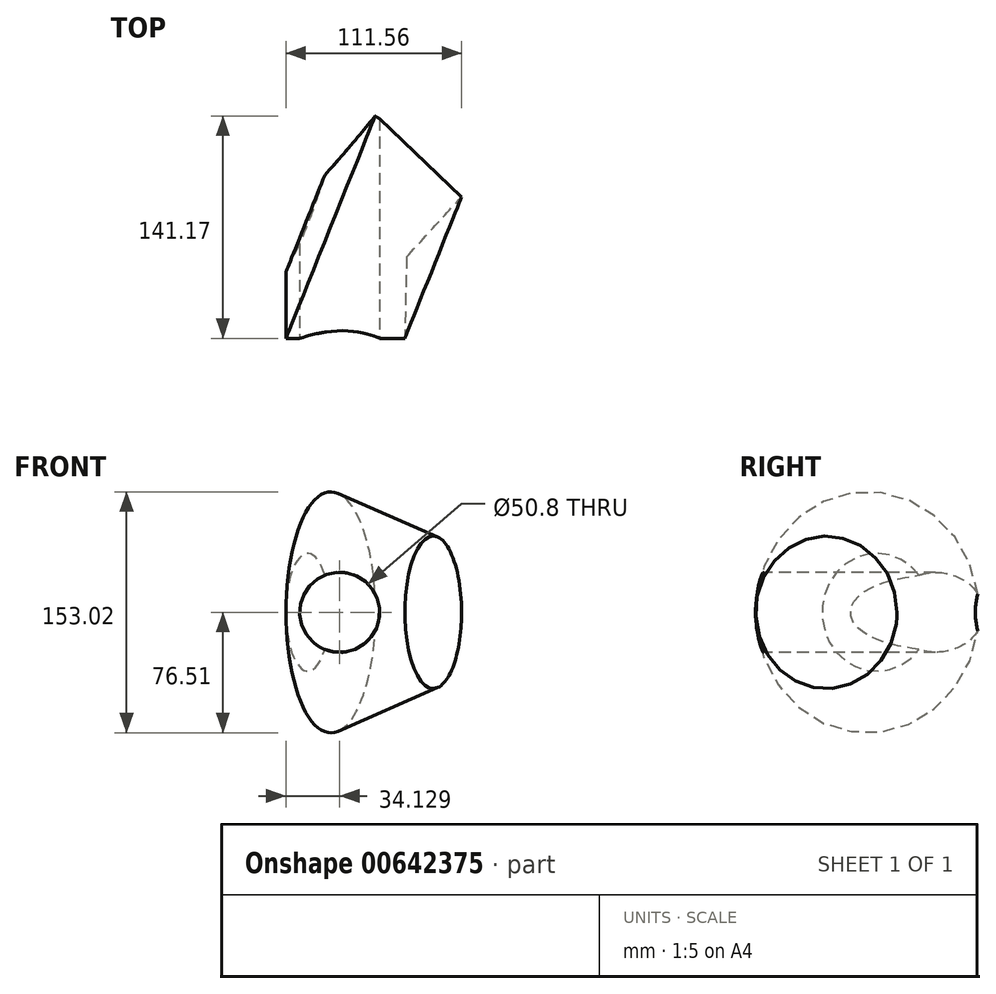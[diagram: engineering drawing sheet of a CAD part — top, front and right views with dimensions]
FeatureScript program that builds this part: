
annotation { "Feature Type Name" : "Feature", "Feature Type Description" : "" }
export const myFeature = defineFeature(function(context is Context, id is Id, definition is map)
    precondition{}
    {
        {
            var Q0;
            Q0=qCreatedBy(makeId("Top.planeOp"),FACE);
            var sketch = newSketch(context, id + "F0", { "sketchPlane" : qUnion([Q0])});
            skLineSegment(sketch, "E0", {"start": v(0, 0) * mm, "end": v(75.52, 0) * mm});
            skLineSegment(sketch, "E1", {"start": v(75.52, 0) * mm, "end": v(76.62, 51.7) * mm});
            skLineSegment(sketch, "E2", {"start": v(76.62, 51.7) * mm, "end": v(16.31, 75.89) * mm});
            skLineSegment(sketch, "E3", {"start": v(16.31, 75.89) * mm, "end": v(0, 42.16) * mm});
            skLineSegment(sketch, "E4", {"start": v(0, 42.16) * mm, "end": v(0, 0) * mm});
            skSolve(sketch);
        }
        {
            var Q0;
            Q0=makeQuery(id+"F0.imprint","IMPRINT",FACE,{"disambiguationData":[TD([[makeQuery(id+"F0.imprint","IMPRINT",EDGE,{"derivedFrom":sQuery(id+"F0.wireOp",EDGE,"E0")}),1.0]])]});
            var Q1;
            Q1=sQuery(id+"F0.wireOp",EDGE,"E2");
            revolve(context, id + "F1", {"entities" : qUnion([Q0]), "axis" : qUnion([Q1]), "revolveType" : RevolveType.FULL});
        }
        {
            var Q0;
            Q0=qCreatedBy(makeId("Front.planeOp"),FACE);
            var sketch = newSketch(context, id + "F2", { "sketchPlane" : qUnion([Q0])});
            skCircle(sketch, "E5", {"center": v(34.13, 0) * mm, "radius": 25.4 * mm});
            skSolve(sketch);
        }
        {
            var Q0;
            Q0=sQuery(id+"F2.wireOp",VERTEX,"E5.center");
            var Q1;
            Q1=makeQuery(id+"F1.opRevolve","SWEPT_BODY",BODY,{"disambiguationData":[OSD([sQuery(id+"F0.wireOp",EDGE,"E0"),sQuery(id+"F0.wireOp",EDGE,"E1"),sQuery(id+"F0.wireOp",EDGE,"E2"),sQuery(id+"F0.wireOp",EDGE,"E3"),sQuery(id+"F0.wireOp",EDGE,"E4")])]});
            hole(context, id + "F3", {"style" : HoleStyle.SIMPLE, "endStyle" : HoleEndStyle.THROUGH, "holeDiameter" : 50.8 * mm, "majorDiameter" : 6.35 * mm, "isTappedThrough" : true, "tappedDepth" : 12.7 * mm, "tapClearance" : 3, "locations" : qUnion([Q0]), "scope" : qUnion([Q1])});
        }
    });
